# Revit family: Legrand XL³-S 630 36 Modules to the  row
name_source: partatom
category: Equipement électrique
units: mm (PartAtom-declared; Revit-internal decimal feet)

## family parameters
Basée sur le plan de construction = Non
Configuration du panneau = Deux colonnes, circuits au sein
Cote de connecteur circulaire = Utiliser le diamètre
Couper avec des vides une fois chargée = Non
Numéro OmniClass = 23.80.30.11.17
Partagée = Non
Point de calcul de pièce = Non
Titre OmniClass = Distribution Boards and Control Panels
Toujours verticalement = Oui
Type d'élément = Tableau de raccordement

## types (11) — shared parameters
Fabricant = Legrand
IK = 08
IP = 40
Image du type = XL3S_630_36M_337583_p_230131.jpg
Material = Steel
RAL = 9003
URL = www.legrand.fr
depth = 249 mm  [stored 0.816929 ft]
depth installation zone = 1053 mm
distance before installation zone = 804 mm  [stored 2.6378 ft]
distance side installation zone = 249 mm  [stored 0.816929 ft]
door = Oui
finish kit = Non
finish kit 337960_337974 = Non
finish kit 337961_337974 = Non
finish kit 337962_337974 = Non
finish kit 337963_337974 = Non
finish kit 337964_337974 = Non
finish kit 337965_337974 = Non
finish kit 337966_337974 = Non
finish kit 337967_337974 = Non
finish kit 337968_337974 = Non
finish kit 337969_337974 = Non
finish kit 337970_337974 = Non
height Base = 100 mm  [stored 0.328084 ft]
left side panel = Oui
plinth = Oui
right side panel = Oui
width = 804 mm  [stored 2.6378 ft]
width installation zone = 1302 mm  [stored 4.27165 ft]
zero-valued in all types: Elévation par défaut

## per-type parameters (varying)
- Distribution envelope - XL³ S 630 Métal - height 750 - 36 modules: Description=Ref 337523 - Distribution envelope - XL³ S 630 Métal - height 750 - 36 modules; General Conditions of Use=https://export.legrand.com; door 337643=Oui; door 337653=Non; door 337663=Non; door 337673=Non; door 337683=Non; door 337693=Non; door 337703=Non; door 337713=Non; door 337723=Non; door 337733=Non; door 337743=Non; envelope 337523=Oui; envelope 337533=Non; envelope 337543=Non; envelope 337553=Non; envelope 337563=Non; envelope 337573=Non; envelope 337583=Non; envelope 337593=Non; envelope 337603=Non; envelope 337613=Non; envelope 337623=Non; height=924 mm  [stored 3.0315 ft]; left side panel 337862=Oui; left side panel 337863=Non; left side panel 337864=Non; left side panel 337865=Non; left side panel 337866=Non; left side panel 337867=Non; left side panel 337868=Non; left side panel 337869=Non; left side panel 337870=Non; left side panel 337871=Non; left side panel 337872=Non; right side panel 337862=Oui; right side panel 337863=Non; right side panel 337864=Non; right side panel 337865=Non; right side panel 337866=Non; right side panel 337867=Non; right side panel 337868=Non; right side panel 337869=Non; right side panel 337870=Non; right side panel 337871=Non; right side panel 337872=Non
- Distribution envelope - XL³ S 630 Métal - height 900 - 36 modules: Description=Ref 337533 - Distribution envelope - XL³ S 630 Métal - height 900 - 36 modules; General Conditions of Use=https://export.legrand.com; door 337643=Non; door 337653=Oui; door 337663=Non; door 337673=Non; door 337683=Non; door 337693=Non; door 337703=Non; door 337713=Non; door 337723=Non; door 337733=Non; door 337743=Non; envelope 337523=Non; envelope 337533=Oui; envelope 337543=Non; envelope 337553=Non; envelope 337563=Non; envelope 337573=Non; envelope 337583=Non; envelope 337593=Non; envelope 337603=Non; envelope 337613=Non; envelope 337623=Non; height=1074 mm  [stored 3.52362 ft]; left side panel 337862=Non; left side panel 337863=Oui; left side panel 337864=Non; left side panel 337865=Non; left side panel 337866=Non; left side panel 337867=Non; left side panel 337868=Non; left side panel 337869=Non; left side panel 337870=Non; left side panel 337871=Non; left side panel 337872=Non; right side panel 337862=Non; right side panel 337863=Oui; right side panel 337864=Non; right side panel 337865=Non; right side panel 337866=Non; right side panel 337867=Non; right side panel 337868=Non; right side panel 337869=Non; right side panel 337870=Non; right side panel 337871=Non; right side panel 337872=Non
- Distribution envelope - XL³ S 630 Métal - height 1050 - 36 modules: Description=Ref 337543 - Distribution envelope - XL³ S 630 Métal - height 1050 - 36 modules; General Conditions of Use=https://export.legrand.com; door 337643=Non; door 337653=Non; door 337663=Oui; door 337673=Non; door 337683=Non; door 337693=Non; door 337703=Non; door 337713=Non; door 337723=Non; door 337733=Non; door 337743=Non; envelope 337523=Non; envelope 337533=Non; envelope 337543=Oui; envelope 337553=Non; envelope 337563=Non; envelope 337573=Non; envelope 337583=Non; envelope 337593=Non; envelope 337603=Non; envelope 337613=Non; envelope 337623=Non; height=1224 mm  [stored 4.01575 ft]; left side panel 337862=Non; left side panel 337863=Non; left side panel 337864=Oui; left side panel 337865=Non; left side panel 337866=Non; left side panel 337867=Non; left side panel 337868=Non; left side panel 337869=Non; left side panel 337870=Non; left side panel 337871=Non; left side panel 337872=Non; right side panel 337862=Non; right side panel 337863=Non; right side panel 337864=Oui; right side panel 337865=Non; right side panel 337866=Non; right side panel 337867=Non; right side panel 337868=Non; right side panel 337869=Non; right side panel 337870=Non; right side panel 337871=Non; right side panel 337872=Non
- Distribution envelope - XL³ S 630 Métal - height 1200 - 36 modules: Description=Ref 337553 - Distribution envelope - XL³ S 630 Métal - height 1200 - 36 modules; General Conditions of Use=https://export.legrand.com; door 337643=Non; door 337653=Non; door 337663=Non; door 337673=Oui; door 337683=Non; door 337693=Non; door 337703=Non; door 337713=Non; door 337723=Non; door 337733=Non; door 337743=Non; envelope 337523=Non; envelope 337533=Non; envelope 337543=Non; envelope 337553=Oui; envelope 337563=Non; envelope 337573=Non; envelope 337583=Non; envelope 337593=Non; envelope 337603=Non; envelope 337613=Non; envelope 337623=Non; height=1374 mm  [stored 4.50787 ft]; left side panel 337862=Non; left side panel 337863=Non; left side panel 337864=Non; left side panel 337865=Oui; left side panel 337866=Non; left side panel 337867=Non; left side panel 337868=Non; left side panel 337869=Non; left side panel 337870=Non; left side panel 337871=Non; left side panel 337872=Non; right side panel 337862=Non; right side panel 337863=Non; right side panel 337864=Non; right side panel 337865=Oui; right side panel 337866=Non; right side panel 337867=Non; right side panel 337868=Non; right side panel 337869=Non; right side panel 337870=Non; right side panel 337871=Non; right side panel 337872=Non
- Distribution envelope - XL³ S 630 Métal - height 1350 - 36 modules: Description=Ref 337563 -Distribution envelope - XL³ S 630 Métal - height 1350 - 36 modules; General Conditions of Use=https://export.legrand.com; door 337643=Non; door 337653=Non; door 337663=Non; door 337673=Non; door 337683=Oui; door 337693=Non; door 337703=Non; door 337713=Non; door 337723=Non; door 337733=Non; door 337743=Non; envelope 337523=Non; envelope 337533=Non; envelope 337543=Non; envelope 337553=Non; envelope 337563=Oui; envelope 337573=Non; envelope 337583=Non; envelope 337593=Non; envelope 337603=Non; envelope 337613=Non; envelope 337623=Non; height=1524 mm  [stored 5 ft]; left side panel 337862=Non; left side panel 337863=Non; left side panel 337864=Non; left side panel 337865=Non; left side panel 337866=Oui; left side panel 337867=Non; left side panel 337868=Non; left side panel 337869=Non; left side panel 337870=Non; left side panel 337871=Non; left side panel 337872=Non; right side panel 337862=Non; right side panel 337863=Non; right side panel 337864=Non; right side panel 337865=Non; right side panel 337866=Oui; right side panel 337867=Non; right side panel 337868=Non; right side panel 337869=Non; right side panel 337870=Non; right side panel 337871=Non; right side panel 337872=Non
- Distribution envelope - XL³ S 630 Métal - height 1500 - 36 modules: Description=Ref 337573 -Distribution envelope - XL³ S 630 Métal - height 1500 - 36 modules; door 337643=Non; door 337653=Non; door 337663=Non; door 337673=Non; door 337683=Non; door 337693=Oui; door 337703=Non; door 337713=Non; door 337723=Non; door 337733=Non; door 337743=Non; envelope 337523=Non; envelope 337533=Non; envelope 337543=Non; envelope 337553=Non; envelope 337563=Non; envelope 337573=Oui; envelope 337583=Non; envelope 337593=Non; envelope 337603=Non; envelope 337613=Non; envelope 337623=Non; height=1674 mm  [stored 5.49213 ft]; left side panel 337862=Non; left side panel 337863=Non; left side panel 337864=Non; left side panel 337865=Non; left side panel 337866=Non; left side panel 337867=Oui; left side panel 337868=Non; left side panel 337869=Non; left side panel 337870=Non; left side panel 337871=Non; left side panel 337872=Non; right side panel 337862=Non; right side panel 337863=Non; right side panel 337864=Non; right side panel 337865=Non; right side panel 337866=Non; right side panel 337867=Oui; right side panel 337868=Non; right side panel 337869=Non; right side panel 337870=Non; right side panel 337871=Non; right side panel 337872=Non
- Distribution envelope - XL³ S 630 Métal - height 1650 - 36 modules: Description=Ref 337583 - Distribution envelope - XL³ S 630 Métal - height 1650 - 36 modules; General Conditions of Use=https://export.legrand.com; door 337643=Non; door 337653=Non; door 337663=Non; door 337673=Non; door 337683=Non; door 337693=Non; door 337703=Oui; door 337713=Non; door 337723=Non; door 337733=Non; door 337743=Non; envelope 337523=Non; envelope 337533=Non; envelope 337543=Non; envelope 337553=Non; envelope 337563=Non; envelope 337573=Non; envelope 337583=Oui; envelope 337593=Non; envelope 337603=Non; envelope 337613=Non; envelope 337623=Non; height=1824 mm  [stored 5.98425 ft]; left side panel 337862=Non; left side panel 337863=Non; left side panel 337864=Non; left side panel 337865=Non; left side panel 337866=Non; left side panel 337867=Non; left side panel 337868=Oui; left side panel 337869=Non; left side panel 337870=Non; left side panel 337871=Non; left side panel 337872=Non; right side panel 337862=Non; right side panel 337863=Non; right side panel 337864=Non; right side panel 337865=Non; right side panel 337866=Non; right side panel 337867=Non; right side panel 337868=Oui; right side panel 337869=Non; right side panel 337870=Non; right side panel 337871=Non; right side panel 337872=Non
- Distribution envelope - XL³ S 630 Métal - height 1800 - 36 modules: Description=Ref 337593 - Distribution envelope - XL³ S 630 Métal - height 1800 - 36 modules; General Conditions of Use=https://export.legrand.com; door 337643=Non; door 337653=Non; door 337663=Non; door 337673=Non; door 337683=Non; door 337693=Non; door 337703=Non; door 337713=Oui; door 337723=Non; door 337733=Non; door 337743=Non; envelope 337523=Non; envelope 337533=Non; envelope 337543=Non; envelope 337553=Non; envelope 337563=Non; envelope 337573=Non; envelope 337583=Non; envelope 337593=Oui; envelope 337603=Non; envelope 337613=Non; envelope 337623=Non; height=1974 mm  [stored 6.47638 ft]; left side panel 337862=Non; left side panel 337863=Non; left side panel 337864=Non; left side panel 337865=Non; left side panel 337866=Non; left side panel 337867=Non; left side panel 337868=Non; left side panel 337869=Oui; left side panel 337870=Non; left side panel 337871=Non; left side panel 337872=Non; right side panel 337862=Non; right side panel 337863=Non; right side panel 337864=Non; right side panel 337865=Non; right side panel 337866=Non; right side panel 337867=Non; right side panel 337868=Non; right side panel 337869=Oui; right side panel 337870=Non; right side panel 337871=Non; right side panel 337872=Non
- Distribution envelope - XL³ S 630 Métal - height 1950 - 36 modules: Description=Ref 337603 - Distribution envelope - XL³ S 630 Métal - height 1950 - 36 modules; General Conditions of Use=https://export.legrand.com; door 337643=Non; door 337653=Non; door 337663=Non; door 337673=Non; door 337683=Non; door 337693=Non; door 337703=Non; door 337713=Non; door 337723=Oui; door 337733=Non; door 337743=Non; envelope 337523=Non; envelope 337533=Non; envelope 337543=Non; envelope 337553=Non; envelope 337563=Non; envelope 337573=Non; envelope 337583=Non; envelope 337593=Non; envelope 337603=Oui; envelope 337613=Non; envelope 337623=Non; height=2124 mm  [stored 6.9685 ft]; left side panel 337862=Non; left side panel 337863=Non; left side panel 337864=Non; left side panel 337865=Non; left side panel 337866=Non; left side panel 337867=Non; left side panel 337868=Non; left side panel 337869=Non; left side panel 337870=Oui; left side panel 337871=Non; left side panel 337872=Non; right side panel 337862=Non; right side panel 337863=Non; right side panel 337864=Non; right side panel 337865=Non; right side panel 337866=Non; right side panel 337867=Non; right side panel 337868=Non; right side panel 337869=Non; right side panel 337870=Oui; right side panel 337871=Non; right side panel 337872=Non
- Distribution envelope - XL³ S 630 Métal - height 2100 - 36 modules: Description=Ref 337613 - Distribution envelope - XL³ S 630 Métal - height 2100 - 36 modules; General Conditions of Use=https://export.legrand.com; door 337643=Non; door 337653=Non; door 337663=Non; door 337673=Non; door 337683=Non; door 337693=Non; door 337703=Non; door 337713=Non; door 337723=Non; door 337733=Oui; door 337743=Non; envelope 337523=Non; envelope 337533=Non; envelope 337543=Non; envelope 337553=Non; envelope 337563=Non; envelope 337573=Non; envelope 337583=Non; envelope 337593=Non; envelope 337603=Non; envelope 337613=Oui; envelope 337623=Non; height=2274 mm  [stored 7.46063 ft]; left side panel 337862=Non; left side panel 337863=Non; left side panel 337864=Non; left side panel 337865=Non; left side panel 337866=Non; left side panel 337867=Non; left side panel 337868=Non; left side panel 337869=Non; left side panel 337870=Non; left side panel 337871=Oui; left side panel 337872=Non; right side panel 337862=Non; right side panel 337863=Non; right side panel 337864=Non; right side panel 337865=Non; right side panel 337866=Non; right side panel 337867=Non; right side panel 337868=Non; right side panel 337869=Non; right side panel 337870=Non; right side panel 337871=Oui; right side panel 337872=Non
- Distribution envelope - XL³ S 630 Métal - height 2250 - 36 modules: Description=Ref 337623 - Distribution envelope - XL³ S 630 Métal - height 2250 - 36 modules; General Conditions of Use=https://export.legrand.com; door 337643=Non; door 337653=Non; door 337663=Non; door 337673=Non; door 337683=Non; door 337693=Non; door 337703=Non; door 337713=Non; door 337723=Non; door 337733=Non; door 337743=Oui; envelope 337523=Non; envelope 337533=Non; envelope 337543=Non; envelope 337553=Non; envelope 337563=Non; envelope 337573=Non; envelope 337583=Non; envelope 337593=Non; envelope 337603=Non; envelope 337613=Non; envelope 337623=Oui; height=2424 mm  [stored 7.95276 ft]; left side panel 337862=Non; left side panel 337863=Non; left side panel 337864=Non; left side panel 337865=Non; left side panel 337866=Non; left side panel 337867=Non; left side panel 337868=Non; left side panel 337869=Non; left side panel 337870=Non; left side panel 337871=Non; left side panel 337872=Oui; right side panel 337862=Non; right side panel 337863=Non; right side panel 337864=Non; right side panel 337865=Non; right side panel 337866=Non; right side panel 337867=Non; right side panel 337868=Non; right side panel 337869=Non; right side panel 337870=Non; right side panel 337871=Non; right side panel 337872=Oui

note: [stored X ft] marks values corroborated as IEEE doubles in the binary element streams (Revit-internal decimal feet)
